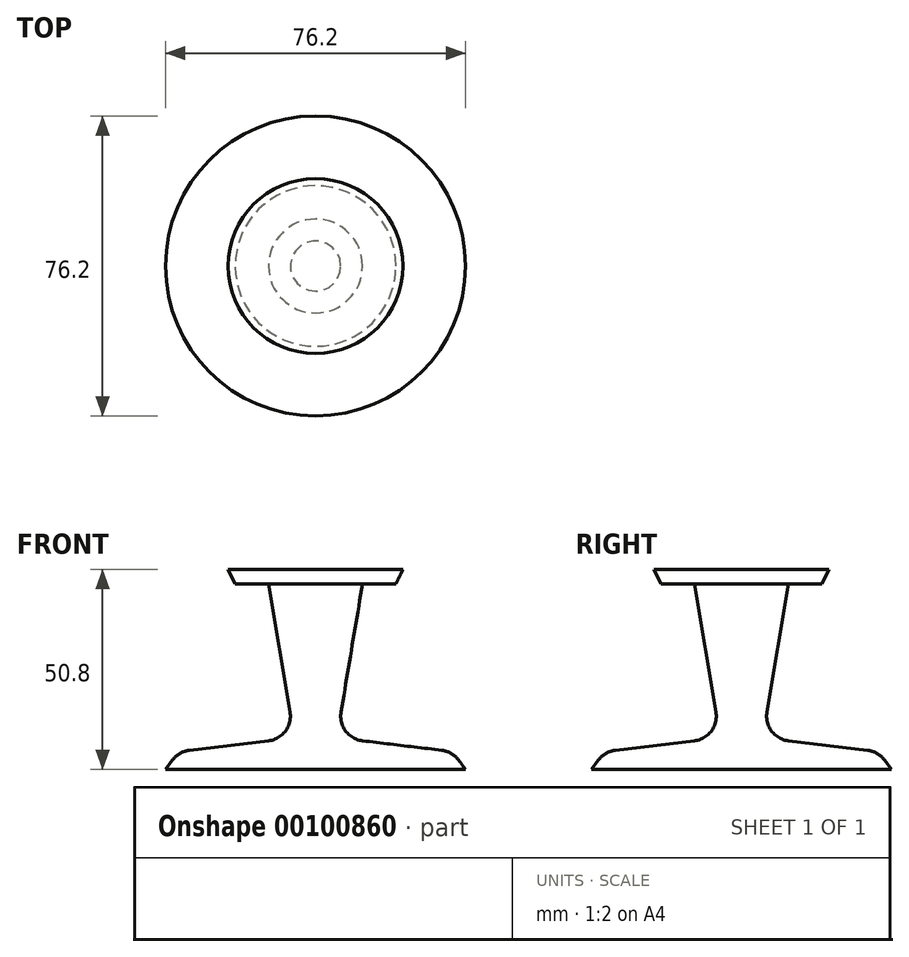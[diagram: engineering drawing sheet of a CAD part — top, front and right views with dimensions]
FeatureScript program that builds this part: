
annotation { "Feature Type Name" : "Feature", "Feature Type Description" : "" }
export const myFeature = defineFeature(function(context is Context, id is Id, definition is map)
    precondition{}
    {
        {
            var Q0;
            Q0=qCreatedBy(makeId("Front.planeOp"),FACE);
            var sketch = newSketch(context, id + "F0", { "sketchPlane" : qUnion([Q0])});
            skLineSegment(sketch, "E0", {"start": v(0, 0) * mm, "end": v(22.22, 0) * mm});
            skLineSegment(sketch, "E1", {"start": v(0, 0) * mm, "end": v(0, -50.8) * mm});
            skLineSegment(sketch, "E2", {"start": v(0, -50.8) * mm, "end": v(38.1, -50.8) * mm});
            skLineSegment(sketch, "E3", {"start": v(38.1, -50.8) * mm, "end": v(36.42, -48.5) * mm});
            skLineSegment(sketch, "E4", {"start": v(32.05, -45.94) * mm, "end": v(12, -43.53) * mm});
            skLineSegment(sketch, "E5", {"start": v(6.49, -36.18) * mm, "end": v(11.93, -3.66) * mm});
            skLineSegment(sketch, "E6", {"start": v(11.93, -3.66) * mm, "end": v(20.4, -3.66) * mm});
            skLineSegment(sketch, "E7", {"start": v(20.4, -3.66) * mm, "end": v(22.23, 0) * mm});
            skPoint(sketch, "E8.visualSharp", {"position": v(5.39, -42.74) * mm});
            skArc(sketch, "E8.filletArc", {"start": v(6.49, -36.18) * mm, "mid": v(7.67, -41.03) * mm, "end": v(12, -43.53) * mm});
            skPoint(sketch, "E9.visualSharp", {"position": v(34.8, -46.27) * mm});
            skArc(sketch, "E9.filletArc", {"start": v(36.42, -48.5) * mm, "mid": v(34.5, -46.76) * mm, "end": v(32.05, -45.94) * mm});
            skSolve(sketch);
        }
        {
            var Q0;
            Q0=makeQuery(id+"F0.imprint","IMPRINT",FACE,{"disambiguationData":[TD([[makeQuery(id+"F0.imprint","IMPRINT",EDGE,{"derivedFrom":sQuery(id+"F0.wireOp",EDGE,"E0")}),-1.0]])]});
            var Q1;
            Q1=sQuery(id+"F0.wireOp",EDGE,"E1");
            revolve(context, id + "F1", {"entities" : qUnion([Q0]), "axis" : qUnion([Q1]), "revolveType" : RevolveType.FULL});
        }
    });
